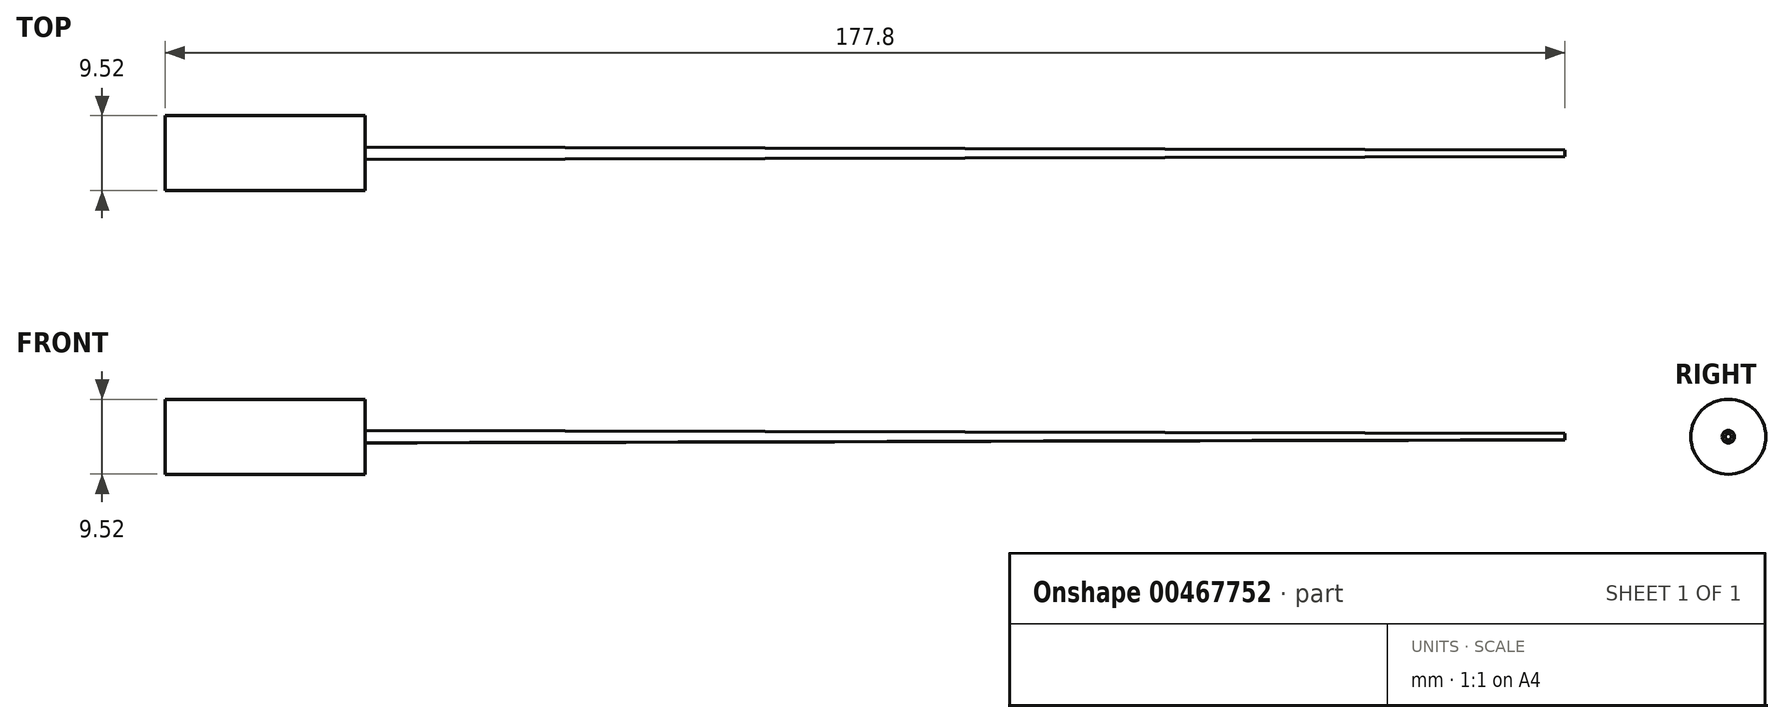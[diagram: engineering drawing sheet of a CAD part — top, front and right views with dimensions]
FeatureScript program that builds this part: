
annotation { "Feature Type Name" : "Feature", "Feature Type Description" : "" }
export const myFeature = defineFeature(function(context is Context, id is Id, definition is map)
    precondition{}
    {
        {
            var Q0;
            Q0=qCreatedBy(makeId("Right.planeOp"),FACE);
            var sketch = newSketch(context, id + "F0", { "sketchPlane" : qUnion([Q0])});
            skCircle(sketch, "E0", {"center": v(0, 0) * mm, "radius": 4.76 * mm});
            skSolve(sketch);
        }
        {
            var Q0;
            Q0 = qSketchRegion(id + "F0", true);
            extrude(context, id + "F1", {"entities" : qUnion([Q0]), "oppositeDirection" : true, "depth" : 25.4 * mm});
        }
        {
            var Q0;
            Q0=makeQuery(id+"F1.opExtrude","CAP_FACE",FACE,{"disambiguationData":[OSD([sQuery(id+"F0.wireOp",EDGE,"E0")])],"isStart":true});
            var sketch = newSketch(context, id + "F2", { "sketchPlane" : qUnion([Q0])});
            skCircle(sketch, "E1", {"center": v(0, 0) * mm, "radius": 0.8 * mm});
            skSolve(sketch);
        }
        {
            var Q0;
            Q0=makeQuery(id+"F2.imprint","IMPRINT",FACE,{"disambiguationData":[TD([[makeQuery(id+"F2.imprint","IMPRINT",EDGE,{"derivedFrom":sQuery(id+"F2.wireOp",EDGE,"E1")}),1.0]])]});
            extrude(context, id + "F3", {"entities" : qUnion([Q0]), "operationType" : NewBodyOperationType.ADD, "depth" : 152.4 * mm, "hasDraft" : true, "draftAngle" : .15 * degree, "draftPullDirection" : true});
        }
    });
